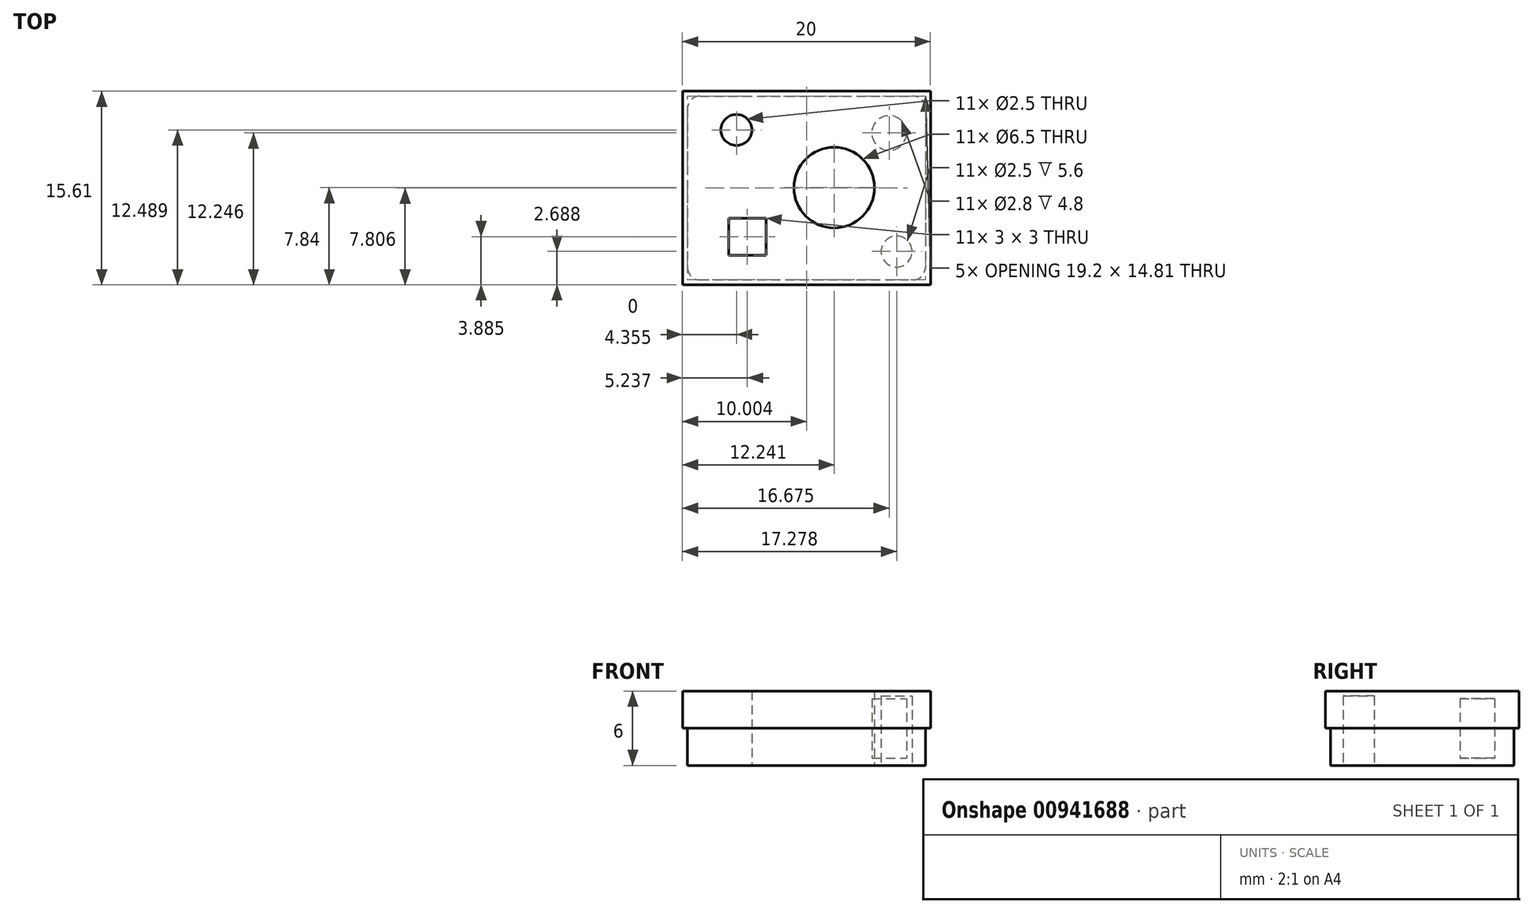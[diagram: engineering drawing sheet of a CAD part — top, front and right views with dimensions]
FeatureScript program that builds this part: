
annotation { "Feature Type Name" : "Feature", "Feature Type Description" : "" }
export const myFeature = defineFeature(function(context is Context, id is Id, definition is map)
    precondition{}
    {
        {
            var Q0;
            Q0=qCreatedBy(makeId("Top.planeOp"),FACE);
            var sketch = newSketch(context, id + "F0", { "sketchPlane" : qUnion([Q0])});
            skLineSegment(sketch, "E0.bottom", {"start": v(-8.57, 7.77) * mm, "end": v(11.43, 7.77) * mm});
            skLineSegment(sketch, "E0.top", {"start": v(-8.57, -7.84) * mm, "end": v(11.43, -7.84) * mm});
            skLineSegment(sketch, "E0.left", {"start": v(-8.57, 7.77) * mm, "end": v(-8.57, -7.84) * mm});
            skLineSegment(sketch, "E0.right", {"start": v(11.43, 7.77) * mm, "end": v(11.43, -7.84) * mm});
            skCircle(sketch, "E1", {"center": v(-4.22, 4.65) * mm, "radius": 1.25 * mm});
            skCircle(sketch, "E2", {"center": v(3.67, 0) * mm, "radius": 3.25 * mm});
            skLineSegment(sketch, "E3.bottom", {"start": v(-4.83, -2.46) * mm, "end": v(-1.83, -2.46) * mm});
            skLineSegment(sketch, "E3.top", {"start": v(-4.83, -5.46) * mm, "end": v(-1.83, -5.46) * mm});
            skLineSegment(sketch, "E3.left", {"start": v(-4.83, -2.46) * mm, "end": v(-4.83, -5.46) * mm});
            skLineSegment(sketch, "E3.right", {"start": v(-1.83, -2.46) * mm, "end": v(-1.83, -5.46) * mm});
            skSolve(sketch);
        }
        {
            var Q0;
            Q0=makeQuery(id+"F0.imprint","IMPRINT",FACE,{"disambiguationData":[TD([[makeQuery(id+"F0.imprint","IMPRINT",EDGE,{"derivedFrom":sQuery(id+"F0.wireOp",EDGE,"E0.bottom")}),-1.0]])]});
            extrude(context, id + "F1", {"entities" : qUnion([Q0]), "depth" : 6 * mm, "offsetDistance" : 25 * mm});
        }
        {
            var Q0;
            Q0=makeQuery(id+"F1.opExtrude","CAP_FACE",FACE,{"disambiguationData":[OSD([sQuery(id+"F0.wireOp",EDGE,"E0.bottom"),sQuery(id+"F0.wireOp",EDGE,"E0.top"),sQuery(id+"F0.wireOp",EDGE,"E0.left"),sQuery(id+"F0.wireOp",EDGE,"E0.right"),sQuery(id+"F0.wireOp",EDGE,"E1"),sQuery(id+"F0.wireOp",EDGE,"E2"),sQuery(id+"F0.wireOp",EDGE,"E3.bottom"),sQuery(id+"F0.wireOp",EDGE,"E3.top"),sQuery(id+"F0.wireOp",EDGE,"E3.left"),sQuery(id+"F0.wireOp",EDGE,"E3.right")])],"isStart":true});
            var sketch = newSketch(context, id + "F2", { "sketchPlane" : qUnion([Q0])});
            skCircle(sketch, "E4", {"center": v(8.7, 5.15) * mm, "radius": 1.25 * mm});
            skSolve(sketch);
        }
        {
            var Q0;
            Q0=makeQuery(id+"F2.imprint","IMPRINT",FACE,{"disambiguationData":[TD([[makeQuery(id+"F2.imprint","IMPRINT",EDGE,{"derivedFrom":sQuery(id+"F2.wireOp",EDGE,"E4")}),1.0]])]});
            extrude(context, id + "F3", {"entities" : qUnion([Q0]), "operationType" : NewBodyOperationType.REMOVE, "oppositeDirection" : true, "depth" : 5.6 * mm, "offsetDistance" : 25 * mm});
        }
        {
            var Q0;
            Q0=makeQuery(id+"F1.opExtrude","CAP_FACE",FACE,{"disambiguationData":[OSD([sQuery(id+"F0.wireOp",EDGE,"E0.bottom"),sQuery(id+"F0.wireOp",EDGE,"E0.top"),sQuery(id+"F0.wireOp",EDGE,"E0.left"),sQuery(id+"F0.wireOp",EDGE,"E0.right"),sQuery(id+"F0.wireOp",EDGE,"E1"),sQuery(id+"F0.wireOp",EDGE,"E2"),sQuery(id+"F0.wireOp",EDGE,"E3.bottom"),sQuery(id+"F0.wireOp",EDGE,"E3.top"),sQuery(id+"F0.wireOp",EDGE,"E3.left"),sQuery(id+"F0.wireOp",EDGE,"E3.right")])],"isStart":true});
            var sketch = newSketch(context, id + "F4", { "sketchPlane" : qUnion([Q0])});
            skLineSegment(sketch, "E5.0", {"start": v(11.03, -7.37) * mm, "end": v(11.03, 7.44) * mm});
            skLineSegment(sketch, "E5.1", {"start": v(-8.17, -7.37) * mm, "end": v(11.03, -7.37) * mm});
            skLineSegment(sketch, "E5.2", {"start": v(-8.17, -7.37) * mm, "end": v(-8.17, 7.44) * mm});
            skLineSegment(sketch, "E5.3", {"start": v(-8.17, 7.44) * mm, "end": v(11.03, 7.44) * mm});
            skLineSegment(sketch, "E6.bottom", {"start": v(11.43, -7.77) * mm, "end": v(-8.57, -7.77) * mm});
            skLineSegment(sketch, "E6.top", {"start": v(11.43, 7.84) * mm, "end": v(-8.57, 7.84) * mm});
            skLineSegment(sketch, "E6.left", {"start": v(11.43, -7.77) * mm, "end": v(11.43, 7.84) * mm});
            skLineSegment(sketch, "E6.right", {"start": v(-8.57, -7.77) * mm, "end": v(-8.57, 7.84) * mm});
            skSolve(sketch);
        }
        {
            var Q0;
            Q0=makeQuery(id+"F4.imprint","IMPRINT",FACE,{"disambiguationData":[TD([[makeQuery(id+"F4.imprint","IMPRINT",EDGE,{"derivedFrom":sQuery(id+"F4.wireOp",EDGE,"E5.0")}),-1.0]])]});
            extrude(context, id + "F5", {"entities" : qUnion([Q0]), "operationType" : NewBodyOperationType.REMOVE, "oppositeDirection" : true, "depth" : 3 * mm, "offsetDistance" : 25 * mm});
        }
        {
            var Q0;
            Q0=makeQuery(id+"F1.opExtrude","CAP_FACE",FACE,{"disambiguationData":[OSD([sQuery(id+"F0.wireOp",EDGE,"E0.bottom"),sQuery(id+"F0.wireOp",EDGE,"E0.top"),sQuery(id+"F0.wireOp",EDGE,"E0.left"),sQuery(id+"F0.wireOp",EDGE,"E0.right"),sQuery(id+"F0.wireOp",EDGE,"E1"),sQuery(id+"F0.wireOp",EDGE,"E2"),sQuery(id+"F0.wireOp",EDGE,"E3.bottom"),sQuery(id+"F0.wireOp",EDGE,"E3.top"),sQuery(id+"F0.wireOp",EDGE,"E3.left"),sQuery(id+"F0.wireOp",EDGE,"E3.right")])],"isStart":true});
            var sketch = newSketch(context, id + "F6", { "sketchPlane" : qUnion([Q0])});
            skCircle(sketch, "E7", {"center": v(8.1, -4.4) * mm, "radius": 1.4 * mm});
            skSolve(sketch);
        }
        {
            var Q0;
            Q0=makeQuery(id+"F6.imprint","IMPRINT",FACE,{"disambiguationData":[TD([[makeQuery(id+"F6.imprint","IMPRINT",EDGE,{"derivedFrom":sQuery(id+"F6.wireOp",EDGE,"E7")}),1.0]])]});
            extrude(context, id + "F7", {"entities" : qUnion([Q0]), "operationType" : NewBodyOperationType.REMOVE, "oppositeDirection" : true, "depth" : 5.4 * mm, "offsetDistance" : 25 * mm, "hasSecondDirection" : true, "secondDirectionOppositeDirection" : false, "secondDirectionDepth" : -.6 * mm});
        }
        {
            var Q0;
            Q0=makeQuery(id+"F5.boolean.opBoolean","COPY",EDGE,{"derivedFrom":makeQuery(id+"F5.opExtrude","SWEPT_EDGE",EDGE,{"disambiguationData":[OSD([sQuery(id+"F4.wireOp",EDGE,"E5.0"),sQuery(id+"F4.wireOp",EDGE,"E5.1")])]})});
            var Q1;
            Q1=makeQuery(id+"F5.boolean.opBoolean","COPY",EDGE,{"derivedFrom":makeQuery(id+"F5.opExtrude","SWEPT_EDGE",EDGE,{"disambiguationData":[OSD([sQuery(id+"F4.wireOp",EDGE,"E5.1"),sQuery(id+"F4.wireOp",EDGE,"E5.2")])]})});
            var Q2;
            Q2=makeQuery(id+"F5.boolean.opBoolean","COPY",EDGE,{"derivedFrom":makeQuery(id+"F5.opExtrude","SWEPT_EDGE",EDGE,{"disambiguationData":[OSD([sQuery(id+"F4.wireOp",EDGE,"E5.2"),sQuery(id+"F4.wireOp",EDGE,"E5.3")])]})});
            var Q3;
            Q3=makeQuery(id+"F5.boolean.opBoolean","COPY",EDGE,{"derivedFrom":makeQuery(id+"F5.opExtrude","SWEPT_EDGE",EDGE,{"disambiguationData":[OSD([sQuery(id+"F4.wireOp",EDGE,"E5.0"),sQuery(id+"F4.wireOp",EDGE,"E5.3")])]})});
            fillet(context, id + "F8", {"entities" : qUnion([Q0, Q1, Q2, Q3]), "radius" : 1 * mm, "tangentPropagation" : true, "allowEdgeOverflow" : false});
        }
    });
